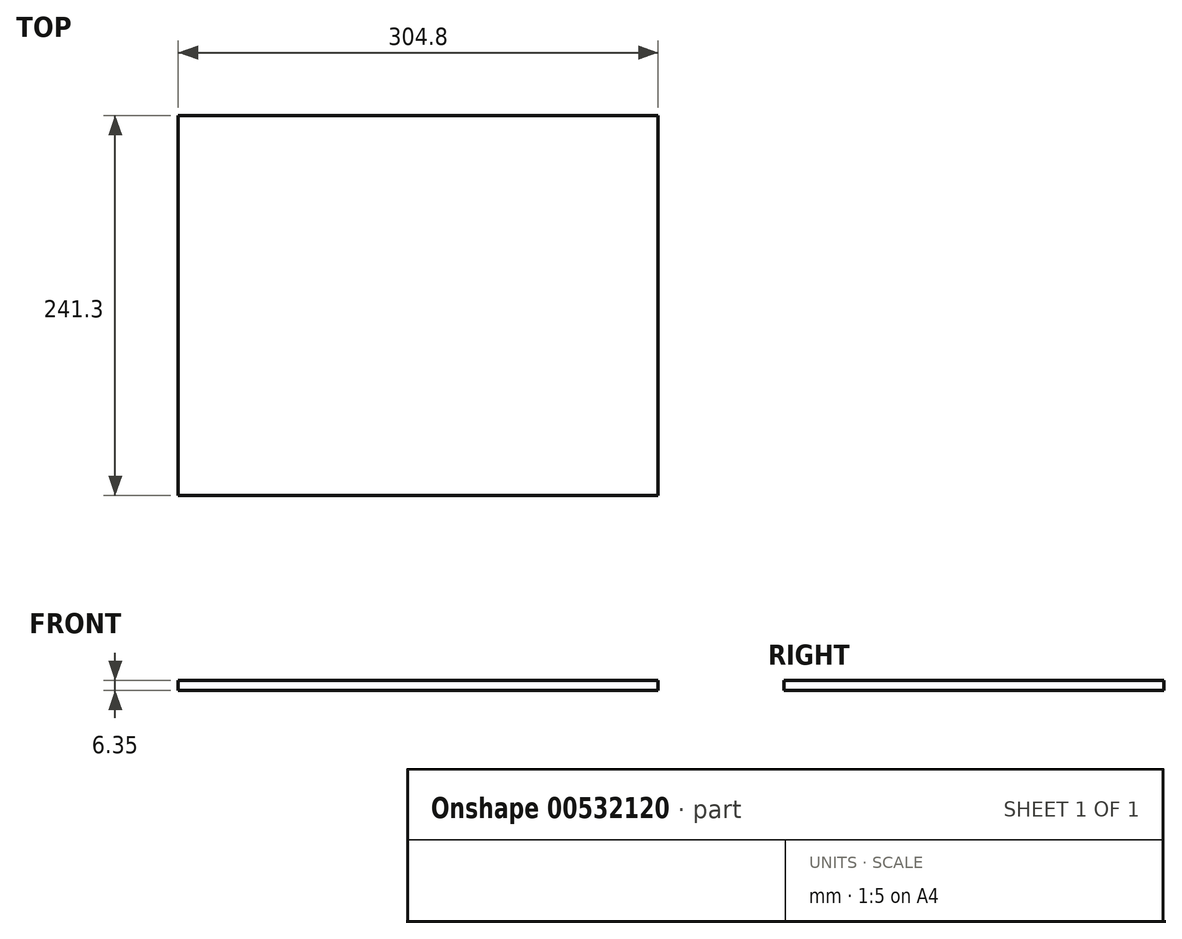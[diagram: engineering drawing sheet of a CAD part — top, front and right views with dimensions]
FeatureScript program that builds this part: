
annotation { "Feature Type Name" : "Feature", "Feature Type Description" : "" }
export const myFeature = defineFeature(function(context is Context, id is Id, definition is map)
    precondition{}
    {
        {
            var Q0;
            Q0=qCreatedBy(makeId("Top.planeOp"),FACE);
            var sketch = newSketch(context, id + "F0", { "sketchPlane" : qUnion([Q0])});
            skLineSegment(sketch, "E0.bottom", {"start": v(152.4, -120.65) * mm, "end": v(-152.4, -120.65) * mm});
            skLineSegment(sketch, "E0.top", {"start": v(152.4, 120.65) * mm, "end": v(-152.4, 120.65) * mm});
            skLineSegment(sketch, "E0.left", {"start": v(152.4, -120.65) * mm, "end": v(152.4, 120.65) * mm});
            skLineSegment(sketch, "E0.right", {"start": v(-152.4, -120.65) * mm, "end": v(-152.4, 120.65) * mm});
            skPoint(sketch, "E0.middle", {"position": v(0, 0) * mm});
            skSolve(sketch);
        }
        {
            var Q0;
            Q0=qSketchRegion(id+"F0",true);
            extrude(context, id + "F1", {"entities" : qUnion([Q0]), "depth" : 6.35 * mm, "offsetDistance" : 25.4 * mm});
        }
    });
